# Revit family: Haworth_Cardigan_Lounge_AP_PRELIMINARY
name_source: partatom
category: Furniture
units: mm (PartAtom-declared; Revit-internal decimal feet)

## family parameters
Always vertical = Yes
Cut with Voids When Loaded = No
OmniClass Number = 23.40.70.14.64.21
OmniClass Title = Systems Furniture
Room Calculation Point = No
Shared = No
Work Plane-Based = No

## types (1)
- Cardigan Lounge
    Actual Depth = 800 mm  [stored 2.62467 ft]
    Actual Height = 970 mm  [stored 3.18241 ft]
    Actual Width = 980 mm  [stored 3.21522 ft]
    Assembly Code = E2020200
    Description = Haworth - Cardigan - Lounge Chair
    Glide Finish = Haworth _ Polymer _ Black
    Manufacturer = Haworth
    Model = Haworth - Cardigan
    Revision Number = 1
    Size = Verify Final Dim. w/ Haworth
    URL = https://www.haworth.com
    Warranty = http://www.haworth.com

note: [stored X ft] marks values corroborated as IEEE doubles in the binary element streams (Revit-internal decimal feet)

## geometry (parser evidence)
native form markers: Sweep x9
no freeform markers — native parametric forms only
